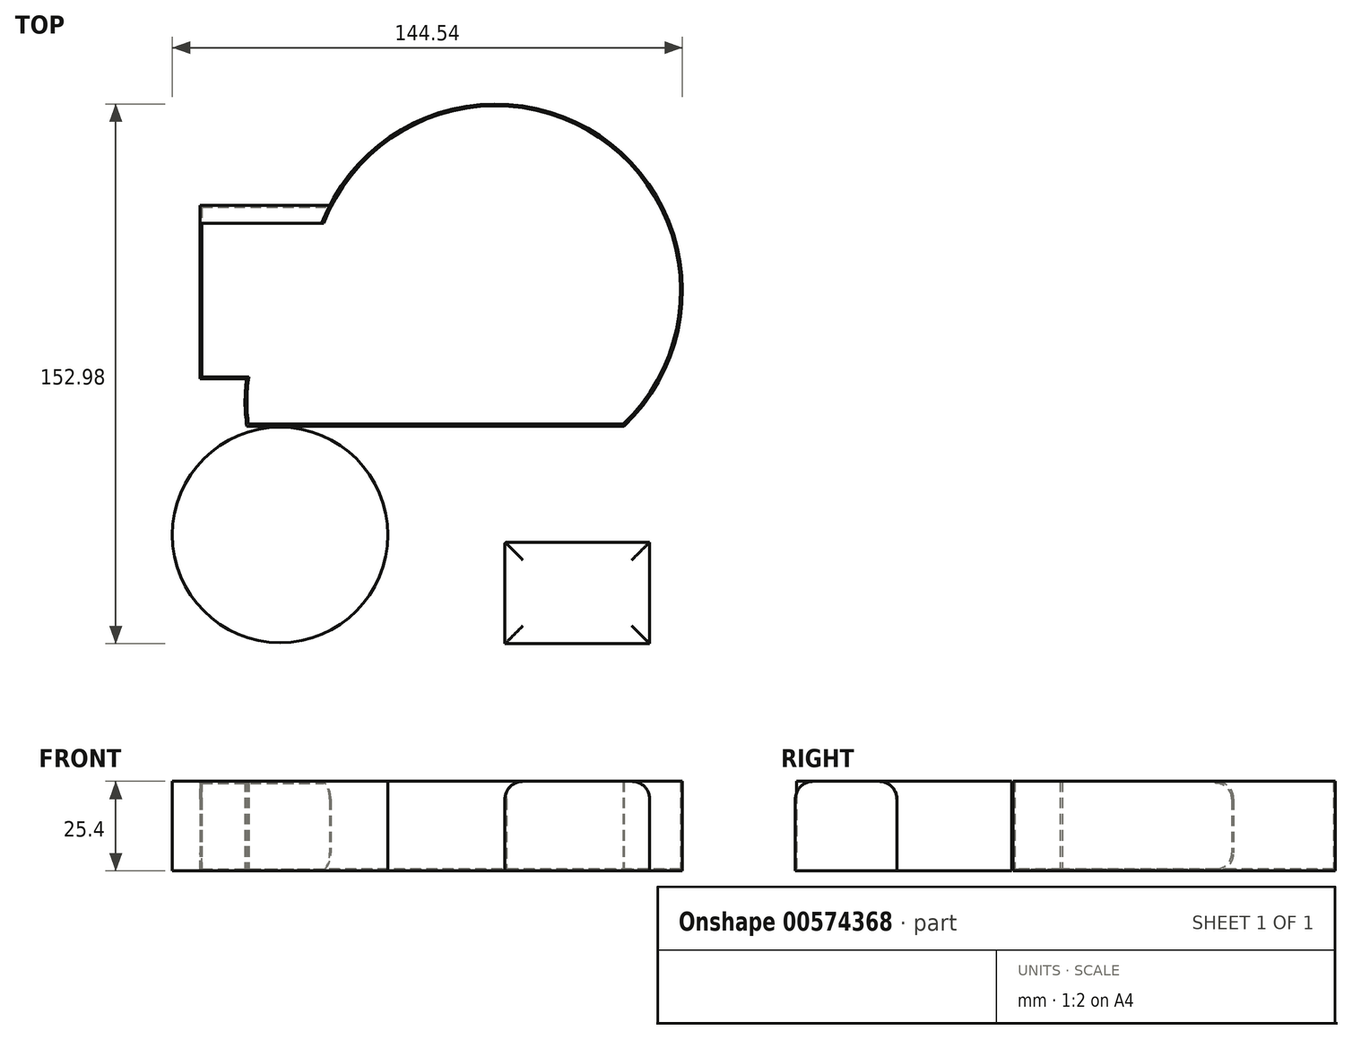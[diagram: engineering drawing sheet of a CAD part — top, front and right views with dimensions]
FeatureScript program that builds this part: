
annotation { "Feature Type Name" : "Feature", "Feature Type Description" : "" }
export const myFeature = defineFeature(function(context is Context, id is Id, definition is map)
    precondition{}
    {
        {
            var Q0;
            Q0=qCreatedBy(makeId("Top.planeOp"),FACE);
            var sketch = newSketch(context, id + "F0", { "sketchPlane" : qUnion([Q0])});
            skCircle(sketch, "E0", {"center": v(18.04, 25.02) * mm, "radius": 52.9 * mm});
            skCircle(sketch, "E1", {"center": v(-43.06, -44.22) * mm, "radius": 30.54 * mm});
            skCircle(sketch, "E2", {"center": v(-5.24, -6.4) * mm, "radius": 47.76 * mm});
            skLineSegment(sketch, "E3.bottom", {"start": v(-65.75, 49.17) * mm, "end": v(61.68, 49.17) * mm});
            skLineSegment(sketch, "E3.top", {"start": v(-65.75, 0) * mm, "end": v(61.68, 0) * mm});
            skLineSegment(sketch, "E3.left", {"start": v(-65.75, 49.17) * mm, "end": v(-65.75, 0) * mm});
            skLineSegment(sketch, "E3.right", {"start": v(61.68, 49.17) * mm, "end": v(61.68, 0) * mm});
            skLineSegment(sketch, "E4.bottom", {"start": v(-70.12, -13.38) * mm, "end": v(75.65, -13.38) * mm});
            skLineSegment(sketch, "E4.top", {"start": v(-70.12, -63.72) * mm, "end": v(75.65, -63.72) * mm});
            skLineSegment(sketch, "E4.left", {"start": v(-70.12, -13.38) * mm, "end": v(-70.12, -63.72) * mm});
            skLineSegment(sketch, "E4.right", {"start": v(75.65, -13.38) * mm, "end": v(75.65, -63.72) * mm});
            skLineSegment(sketch, "E5.bottom", {"start": v(61.68, -46.26) * mm, "end": v(20.66, -46.26) * mm});
            skLineSegment(sketch, "E5.top", {"start": v(61.68, -75.06) * mm, "end": v(20.66, -75.06) * mm});
            skLineSegment(sketch, "E5.left", {"start": v(61.68, -46.26) * mm, "end": v(61.68, -75.06) * mm});
            skLineSegment(sketch, "E5.right", {"start": v(20.66, -46.26) * mm, "end": v(20.66, -75.06) * mm});
            skSolve(sketch);
        }
        {
            var Q0;
            {var subQ0=sQuery(id+"F0.wireOp",EDGE,"E3.right");Q0=makeQuery(id+"F0.imprint","IMPRINT",FACE,{"disambiguationData":[TD([[makeQuery(id+"F0.imprint","IMPRINT",EDGE,{"derivedFrom":subQ0}),-1.0]])]});}
            var Q1;
            {var subQ0=sQuery(id+"F0.wireOp",EDGE,"E3.right");Q1=makeQuery(id+"F0.imprint","IMPRINT",FACE,{"disambiguationData":[TD([[makeQuery(id+"F0.imprint","IMPRINT",EDGE,{"derivedFrom":subQ0}),1.0]])]});}
            var Q2;
            {var subQ0=sQuery(id+"F0.wireOp",EDGE,"E2");var subQ1=sQuery(id+"F0.wireOp",EDGE,"E0");var subQ2=makeQuery(id+"F0.imprint","INTERSECT",VERTEX,{"disambiguationData":[OD(0.0)],"derivedFrom":[subQ1,subQ0]});Q2=makeQuery(id+"F0.imprint","IMPRINT",FACE,{"disambiguationData":[TD([[makeQuery(id+"F0.imprint","IMPRINT",EDGE,{"disambiguationData":[TD([[subQ2,-1.0]])],"derivedFrom":subQ1}),1.0]])]});}
            var Q3;
            {var subQ0=sQuery(id+"F0.wireOp",EDGE,"E3.top");var subQ1=sQuery(id+"F0.wireOp",EDGE,"E0");var subQ2=makeQuery(id+"F0.imprint","INTERSECT",VERTEX,{"derivedFrom":[subQ1,subQ0]});Q3=makeQuery(id+"F0.imprint","IMPRINT",FACE,{"disambiguationData":[TD([[makeQuery(id+"F0.imprint","IMPRINT",EDGE,{"disambiguationData":[TD([[subQ2,-1.0]])],"derivedFrom":subQ1}),-1.0]])]});}
            var Q4;
            {var subQ5=sQuery(id+"F0.wireOp",EDGE,"E4.bottom");var subQ8=sQuery(id+"F0.wireOp",EDGE,"E0");var subQ9=makeQuery(id+"F0.imprint","INTERSECT",VERTEX,{"disambiguationData":[OD(1.0)],"derivedFrom":[subQ8,subQ5]});Q4=makeQuery(id+"F0.imprint","IMPRINT",FACE,{"disambiguationData":[TD([[makeQuery(id+"F0.imprint","IMPRINT",EDGE,{"disambiguationData":[TD([[subQ9,-1.0]])],"derivedFrom":subQ8}),-1.0]])]});}
            var Q5;
            {var subQ0=sQuery(id+"F0.wireOp",EDGE,"E3.left");Q5=makeQuery(id+"F0.imprint","IMPRINT",FACE,{"disambiguationData":[TD([[makeQuery(id+"F0.imprint","IMPRINT",EDGE,{"derivedFrom":subQ0}),1.0]])]});}
            var Q6;
            {var subQ0=sQuery(id+"F0.wireOp",EDGE,"E2");var subQ1=sQuery(id+"F0.wireOp",EDGE,"E0");var subQ2=makeQuery(id+"F0.imprint","INTERSECT",VERTEX,{"disambiguationData":[OD(0.0)],"derivedFrom":[subQ1,subQ0]});Q6=makeQuery(id+"F0.imprint","IMPRINT",FACE,{"disambiguationData":[TD([[makeQuery(id+"F0.imprint","IMPRINT",EDGE,{"disambiguationData":[TD([[subQ2,-1.0]])],"derivedFrom":subQ1}),-1.0]])]});}
            var Q7;
            {var subQ0=sQuery(id+"F0.wireOp",EDGE,"E3.top");var subQ1=sQuery(id+"F0.wireOp",EDGE,"E0");var subQ2=makeQuery(id+"F0.imprint","INTERSECT",VERTEX,{"derivedFrom":[subQ1,subQ0]});Q7=makeQuery(id+"F0.imprint","IMPRINT",FACE,{"disambiguationData":[TD([[makeQuery(id+"F0.imprint","IMPRINT",EDGE,{"disambiguationData":[TD([[subQ2,-1.0]])],"derivedFrom":subQ1}),1.0]])]});}
            var Q8;
            {var subQ0=sQuery(id+"F0.wireOp",EDGE,"E4.bottom");var subQ1=sQuery(id+"F0.wireOp",EDGE,"E0");var subQ2=makeQuery(id+"F0.imprint","INTERSECT",VERTEX,{"disambiguationData":[OD(1.0)],"derivedFrom":[subQ1,subQ0]});Q8=makeQuery(id+"F0.imprint","IMPRINT",FACE,{"disambiguationData":[TD([[makeQuery(id+"F0.imprint","IMPRINT",EDGE,{"disambiguationData":[TD([[subQ2,-1.0]])],"derivedFrom":subQ1}),1.0]])]});}
            var Q9;
            {var subQ5=sQuery(id+"F0.wireOp",EDGE,"E2");var subQ7=sQuery(id+"F0.wireOp",EDGE,"E5.right");var subQ9=makeQuery(id+"F0.imprint","INTERSECT",VERTEX,{"derivedFrom":[subQ5,subQ7]});Q9=makeQuery(id+"F0.imprint","IMPRINT",FACE,{"disambiguationData":[TD([[makeQuery(id+"F0.imprint","IMPRINT",EDGE,{"disambiguationData":[TD([[subQ9,-1.0]])],"derivedFrom":subQ5}),-1.0]])]});}
            var Q10;
            {var subQ1=sQuery(id+"F0.wireOp",EDGE,"E1");var subQ5=sQuery(id+"F0.wireOp",EDGE,"E4.left");var subQ8=makeQuery(id+"F0.imprint","INTERSECT",VERTEX,{"disambiguationData":[OD(0.0)],"derivedFrom":[subQ1,subQ5]});Q10=makeQuery(id+"F0.imprint","IMPRINT",FACE,{"disambiguationData":[TD([[makeQuery(id+"F0.imprint","IMPRINT",EDGE,{"disambiguationData":[TD([[subQ8,1.0]])],"derivedFrom":subQ1}),1.0]])]});}
            var Q11;
            {var subQ0=sQuery(id+"F0.wireOp",EDGE,"E2");var subQ1=sQuery(id+"F0.wireOp",EDGE,"E1");var subQ2=makeQuery(id+"F0.imprint","INTERSECT",VERTEX,{"disambiguationData":[OD(0.0)],"derivedFrom":[subQ1,subQ0]});Q11=makeQuery(id+"F0.imprint","IMPRINT",FACE,{"disambiguationData":[TD([[makeQuery(id+"F0.imprint","IMPRINT",EDGE,{"disambiguationData":[TD([[subQ2,1.0]])],"derivedFrom":subQ1}),1.0]])]});}
            var Q12;
            {var subQ0=sQuery(id+"F0.wireOp",EDGE,"E4.bottom");var subQ1=sQuery(id+"F0.wireOp",EDGE,"E0");var subQ2=makeQuery(id+"F0.imprint","INTERSECT",VERTEX,{"disambiguationData":[OD(0.0)],"derivedFrom":[subQ1,subQ0]});Q12=makeQuery(id+"F0.imprint","IMPRINT",FACE,{"disambiguationData":[TD([[makeQuery(id+"F0.imprint","IMPRINT",EDGE,{"disambiguationData":[TD([[subQ2,1.0]])],"derivedFrom":subQ1}),1.0]])]});}
            var Q13;
            {var subQ5=sQuery(id+"F0.wireOp",EDGE,"E5.top");Q13=makeQuery(id+"F0.imprint","IMPRINT",FACE,{"disambiguationData":[TD([[makeQuery(id+"F0.imprint","IMPRINT",EDGE,{"derivedFrom":subQ5}),-1.0]])]});}
            var Q14;
            {var subQ0=sQuery(id+"F0.wireOp",EDGE,"E4.top");var subQ1=sQuery(id+"F0.wireOp",EDGE,"E1");var subQ2=makeQuery(id+"F0.imprint","INTERSECT",VERTEX,{"disambiguationData":[OD(0.0)],"derivedFrom":[subQ1,subQ0]});Q14=makeQuery(id+"F0.imprint","IMPRINT",FACE,{"disambiguationData":[TD([[makeQuery(id+"F0.imprint","IMPRINT",EDGE,{"disambiguationData":[TD([[subQ2,-1.0]])],"derivedFrom":subQ1}),1.0]])]});}
            var Q15;
            {var subQ0=sQuery(id+"F0.wireOp",EDGE,"E4.left");var subQ1=sQuery(id+"F0.wireOp",EDGE,"E1");var subQ2=makeQuery(id+"F0.imprint","INTERSECT",VERTEX,{"disambiguationData":[OD(0.0)],"derivedFrom":[subQ1,subQ0]});Q15=makeQuery(id+"F0.imprint","IMPRINT",FACE,{"disambiguationData":[TD([[makeQuery(id+"F0.imprint","IMPRINT",EDGE,{"disambiguationData":[TD([[subQ2,-1.0]])],"derivedFrom":subQ1}),1.0]])]});}
            extrude(context, id + "F1", {"entities" : qUnion([Q0, Q1, Q2, Q3, Q4, Q5, Q6, Q7, Q8, Q9, Q10, Q11, Q12, Q13, Q14, Q15]), "depth" : 25.4 * mm, "offsetDistance" : 25.4 * mm});
        }
        {
            var Q0;
            Q0=makeQuery(id+"F1.opExtrude","CAP_EDGE",EDGE,{"disambiguationData":[OSD([sQuery(id+"F0.wireOp",EDGE,"E3.bottom")])],"isStart":false});
            var Q1;
            Q1=makeQuery(id+"F1.opExtrude","CAP_EDGE",EDGE,{"disambiguationData":[OSD([sQuery(id+"F0.wireOp",EDGE,"E3.bottom")])],"isStart":true});
            var Q2;
            {var subQ0=sQuery(id+"F0.wireOp",EDGE,"E5.bottom");Q2=makeQuery(id+"F1.opExtrude","CAP_EDGE",EDGE,{"disambiguationData":[OSD([subQ0]),TDD([makeQuery(id+"F0.imprint","IMPRINT",EDGE,{"disambiguationData":[TD([[makeQuery(id+"F0.imprint","INTERSECT",VERTEX,{"derivedFrom":[subQ0,sQuery(id+"F0.wireOp",EDGE,"E5.left")]}),-1.0]])],"derivedFrom":subQ0})])],"isStart":false});}
            var Q3;
            Q3=makeQuery(id+"F1.opExtrude","CAP_EDGE",EDGE,{"disambiguationData":[OSD([sQuery(id+"F0.wireOp",EDGE,"E5.left")])],"isStart":false});
            var Q4;
            Q4=makeQuery(id+"F1.opExtrude","CAP_EDGE",EDGE,{"disambiguationData":[OSD([sQuery(id+"F0.wireOp",EDGE,"E5.top")])],"isStart":false});
            var Q5;
            {var subQ0=sQuery(id+"F0.wireOp",EDGE,"E5.right");var subQ1=makeQuery(id+"F0.imprint","INTERSECT",VERTEX,{"derivedFrom":[sQuery(id+"F0.wireOp",EDGE,"E4.top"),subQ0]});Q5=makeQuery(id+"F1.opExtrude","CAP_EDGE",EDGE,{"disambiguationData":[OSD([subQ0]),TDD([makeQuery(id+"F0.imprint","IMPRINT",EDGE,{"disambiguationData":[TD([[subQ1,1.0]])],"derivedFrom":subQ0}),makeQuery(id+"F0.imprint","IMPRINT",EDGE,{"disambiguationData":[TD([[makeQuery(id+"F0.imprint","INTERSECT",VERTEX,{"derivedFrom":[sQuery(id+"F0.wireOp",EDGE,"E5.top"),subQ0]}),1.0]])],"derivedFrom":subQ0})])],"isStart":false});}
            fillet(context, id + "F2", {"entities" : qUnion([Q0, Q1, Q2, Q3, Q4, Q5]), "radius" : 5.08 * mm, "tangentPropagation" : true, "allowEdgeOverflow" : false});
        }
        {
            var Q0;
            Q0=makeQuery(id+"F1.opExtrude","CAP_FACE",FACE,{"disambiguationData":[OSD([sQuery(id+"F0.wireOp",EDGE,"E0"),sQuery(id+"F0.wireOp",EDGE,"E1"),sQuery(id+"F0.wireOp",EDGE,"E2"),sQuery(id+"F0.wireOp",EDGE,"E3.bottom"),sQuery(id+"F0.wireOp",EDGE,"E3.top"),sQuery(id+"F0.wireOp",EDGE,"E3.left"),sQuery(id+"F0.wireOp",EDGE,"E5.bottom"),sQuery(id+"F0.wireOp",EDGE,"E5.right")])],"isStart":false});
            shell(context, id + "F3", {"entities" : qUnion([Q0]), "thickness" : 0.54 * mm});
        }
    });
